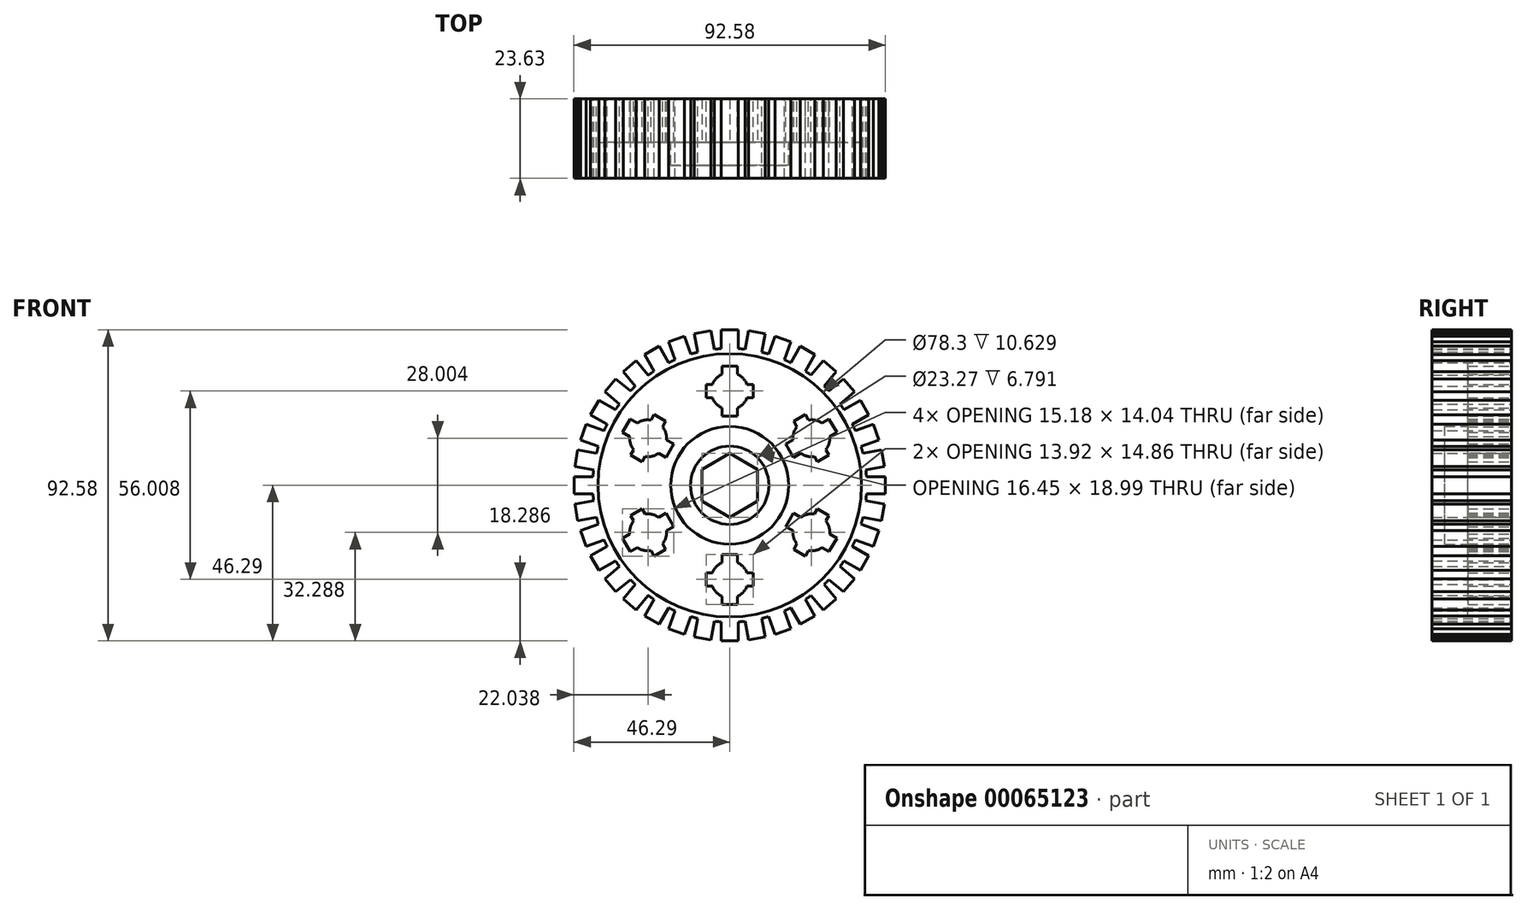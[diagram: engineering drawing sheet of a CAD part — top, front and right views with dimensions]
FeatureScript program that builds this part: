
annotation { "Feature Type Name" : "Feature", "Feature Type Description" : "" }
export const myFeature = defineFeature(function(context is Context, id is Id, definition is map)
    precondition{}
    {
        {
            var Q0;
            Q0=qCreatedBy(makeId("Front.planeOp"),FACE);
            var sketch = newSketch(context, id + "F0", { "sketchPlane" : qUnion([Q0])});
            skCircle(sketch, "E0", {"center": v(0, 0) * mm, "radius": 40.7 * mm});
            skLineSegment(sketch, "E1", {"start": v(-2.5, 40.63) * mm, "end": v(-2.5, 46.29) * mm});
            skLineSegment(sketch, "E2", {"start": v(-2.5, 46.29) * mm, "end": v(0, 46.29) * mm});
            skLineSegment(sketch, "E3", {"start": v(0, 46.29) * mm, "end": v(0, 40.7) * mm});
            skLineSegment(sketch, "E4", {"start": v(0, 40.7) * mm, "end": v(-2.5, 40.63) * mm});
            skLineSegment(sketch, "E5.MirrorCS", {"start": v(2.5, 40.63) * mm, "end": v(2.5, 46.29) * mm});
            skLineSegment(sketch, "E6.MirrorCS", {"start": v(2.5, 46.29) * mm, "end": v(0, 46.29) * mm});
            skLineSegment(sketch, "E7.MirrorCS", {"start": v(0, 40.7) * mm, "end": v(2.5, 40.63) * mm});
            skLineSegment(sketch, "E8.1.0", {"start": v(-4.58, 40.45) * mm, "end": v(-5.57, 46.02) * mm});
            skLineSegment(sketch, "E8.1.1", {"start": v(-10.5, 45.15) * mm, "end": v(-8.04, 45.58) * mm});
            skLineSegment(sketch, "E8.1.2", {"start": v(-8.04, 45.58) * mm, "end": v(-7.07, 40.09) * mm});
            skLineSegment(sketch, "E8.1.3", {"start": v(-5.57, 46.02) * mm, "end": v(-8.04, 45.58) * mm});
            skLineSegment(sketch, "E8.1.4", {"start": v(-9.53, 39.57) * mm, "end": v(-10.5, 45.15) * mm});
            skLineSegment(sketch, "E8.2.0", {"start": v(-11.54, 39.03) * mm, "end": v(-13.47, 44.35) * mm});
            skLineSegment(sketch, "E8.2.1", {"start": v(-18.19, 42.64) * mm, "end": v(-15.83, 43.5) * mm});
            skLineSegment(sketch, "E8.2.2", {"start": v(-15.83, 43.5) * mm, "end": v(-13.92, 38.25) * mm});
            skLineSegment(sketch, "E8.2.3", {"start": v(-13.47, 44.35) * mm, "end": v(-15.83, 43.5) * mm});
            skLineSegment(sketch, "E8.2.4", {"start": v(-16.25, 37.32) * mm, "end": v(-18.19, 42.64) * mm});
            skLineSegment(sketch, "E8.3.0", {"start": v(-18.14, 36.44) * mm, "end": v(-20.97, 41.34) * mm});
            skLineSegment(sketch, "E8.3.1", {"start": v(-25.32, 38.83) * mm, "end": v(-23.14, 40.08) * mm});
            skLineSegment(sketch, "E8.3.2", {"start": v(-23.14, 40.08) * mm, "end": v(-20.35, 35.25) * mm});
            skLineSegment(sketch, "E8.3.3", {"start": v(-20.97, 41.34) * mm, "end": v(-23.14, 40.08) * mm});
            skLineSegment(sketch, "E8.3.4", {"start": v(-22.49, 33.93) * mm, "end": v(-25.32, 38.83) * mm});
            skLineSegment(sketch, "E9.1.4.0", {"start": v(-24.2, 32.73) * mm, "end": v(-27.83, 37.07) * mm});
            skLineSegment(sketch, "E9.3.4.0", {"start": v(-31.67, 33.84) * mm, "end": v(-29.75, 35.46) * mm});
            skLineSegment(sketch, "E9.6.4.0", {"start": v(-29.75, 35.46) * mm, "end": v(-26.16, 31.18) * mm});
            skLineSegment(sketch, "E9.9.4.0", {"start": v(-27.83, 37.07) * mm, "end": v(-29.75, 35.46) * mm});
            skLineSegment(sketch, "E9.12.4.0", {"start": v(-28.04, 29.5) * mm, "end": v(-31.67, 33.84) * mm});
            skLineSegment(sketch, "E9.1.5.0", {"start": v(-29.5, 28.04) * mm, "end": v(-33.84, 31.67) * mm});
            skLineSegment(sketch, "E9.3.5.0", {"start": v(-37.07, 27.83) * mm, "end": v(-35.46, 29.75) * mm});
            skLineSegment(sketch, "E9.6.5.0", {"start": v(-35.46, 29.75) * mm, "end": v(-31.18, 26.16) * mm});
            skLineSegment(sketch, "E9.9.5.0", {"start": v(-33.84, 31.67) * mm, "end": v(-35.46, 29.75) * mm});
            skLineSegment(sketch, "E9.12.5.0", {"start": v(-32.73, 24.2) * mm, "end": v(-37.07, 27.83) * mm});
            skLineSegment(sketch, "E9.1.6.0", {"start": v(-33.93, 22.49) * mm, "end": v(-38.83, 25.32) * mm});
            skLineSegment(sketch, "E9.3.6.0", {"start": v(-41.34, 20.97) * mm, "end": v(-40.08, 23.14) * mm});
            skLineSegment(sketch, "E9.6.6.0", {"start": v(-40.08, 23.14) * mm, "end": v(-35.25, 20.35) * mm});
            skLineSegment(sketch, "E9.9.6.0", {"start": v(-38.83, 25.32) * mm, "end": v(-40.08, 23.14) * mm});
            skLineSegment(sketch, "E9.12.6.0", {"start": v(-36.44, 18.14) * mm, "end": v(-41.34, 20.97) * mm});
            skLineSegment(sketch, "E9.1.7.0", {"start": v(-37.32, 16.25) * mm, "end": v(-42.64, 18.19) * mm});
            skLineSegment(sketch, "E9.3.7.0", {"start": v(-44.35, 13.47) * mm, "end": v(-43.5, 15.83) * mm});
            skLineSegment(sketch, "E9.6.7.0", {"start": v(-43.5, 15.83) * mm, "end": v(-38.25, 13.92) * mm});
            skLineSegment(sketch, "E9.9.7.0", {"start": v(-42.64, 18.19) * mm, "end": v(-43.5, 15.83) * mm});
            skLineSegment(sketch, "E9.12.7.0", {"start": v(-39.03, 11.54) * mm, "end": v(-44.35, 13.47) * mm});
            skLineSegment(sketch, "E9.1.8.0", {"start": v(-39.57, 9.53) * mm, "end": v(-45.15, 10.5) * mm});
            skLineSegment(sketch, "E9.3.8.0", {"start": v(-46.02, 5.57) * mm, "end": v(-45.58, 8.04) * mm});
            skLineSegment(sketch, "E9.6.8.0", {"start": v(-45.58, 8.04) * mm, "end": v(-40.09, 7.07) * mm});
            skLineSegment(sketch, "E9.9.8.0", {"start": v(-45.15, 10.5) * mm, "end": v(-45.58, 8.04) * mm});
            skLineSegment(sketch, "E9.12.8.0", {"start": v(-40.45, 4.58) * mm, "end": v(-46.02, 5.57) * mm});
            skLineSegment(sketch, "E9.1.9.0", {"start": v(-40.63, 2.5) * mm, "end": v(-46.29, 2.5) * mm});
            skLineSegment(sketch, "E9.3.9.0", {"start": v(-46.29, -2.5) * mm, "end": v(-46.29, 0) * mm});
            skLineSegment(sketch, "E9.6.9.0", {"start": v(-46.29, 0) * mm, "end": v(-40.7, 0) * mm});
            skLineSegment(sketch, "E9.9.9.0", {"start": v(-46.29, 2.5) * mm, "end": v(-46.29, 0) * mm});
            skLineSegment(sketch, "E9.12.9.0", {"start": v(-40.63, -2.5) * mm, "end": v(-46.29, -2.5) * mm});
            skLineSegment(sketch, "E9.1.10.0", {"start": v(-40.45, -4.58) * mm, "end": v(-46.02, -5.57) * mm});
            skLineSegment(sketch, "E9.3.10.0", {"start": v(-45.15, -10.5) * mm, "end": v(-45.58, -8.04) * mm});
            skLineSegment(sketch, "E9.6.10.0", {"start": v(-45.58, -8.04) * mm, "end": v(-40.09, -7.07) * mm});
            skLineSegment(sketch, "E9.9.10.0", {"start": v(-46.02, -5.57) * mm, "end": v(-45.58, -8.04) * mm});
            skLineSegment(sketch, "E9.12.10.0", {"start": v(-39.57, -9.53) * mm, "end": v(-45.15, -10.5) * mm});
            skLineSegment(sketch, "E9.1.11.0", {"start": v(-39.03, -11.54) * mm, "end": v(-44.35, -13.47) * mm});
            skLineSegment(sketch, "E9.3.11.0", {"start": v(-42.64, -18.19) * mm, "end": v(-43.5, -15.83) * mm});
            skLineSegment(sketch, "E9.6.11.0", {"start": v(-43.5, -15.83) * mm, "end": v(-38.25, -13.92) * mm});
            skLineSegment(sketch, "E9.9.11.0", {"start": v(-44.35, -13.47) * mm, "end": v(-43.5, -15.83) * mm});
            skLineSegment(sketch, "E9.12.11.0", {"start": v(-37.32, -16.25) * mm, "end": v(-42.64, -18.19) * mm});
            skLineSegment(sketch, "E10.1.12.0", {"start": v(-36.44, -18.14) * mm, "end": v(-41.34, -20.97) * mm});
            skLineSegment(sketch, "E10.3.12.0", {"start": v(-38.83, -25.32) * mm, "end": v(-40.08, -23.14) * mm});
            skLineSegment(sketch, "E10.6.12.0", {"start": v(-40.08, -23.14) * mm, "end": v(-35.25, -20.35) * mm});
            skLineSegment(sketch, "E10.9.12.0", {"start": v(-41.34, -20.97) * mm, "end": v(-40.08, -23.14) * mm});
            skLineSegment(sketch, "E10.12.12.0", {"start": v(-33.93, -22.49) * mm, "end": v(-38.83, -25.32) * mm});
            skLineSegment(sketch, "E10.1.13.0", {"start": v(-32.73, -24.2) * mm, "end": v(-37.07, -27.83) * mm});
            skLineSegment(sketch, "E10.3.13.0", {"start": v(-33.84, -31.67) * mm, "end": v(-35.46, -29.75) * mm});
            skLineSegment(sketch, "E10.6.13.0", {"start": v(-35.46, -29.75) * mm, "end": v(-31.18, -26.16) * mm});
            skLineSegment(sketch, "E10.9.13.0", {"start": v(-37.07, -27.83) * mm, "end": v(-35.46, -29.75) * mm});
            skLineSegment(sketch, "E10.12.13.0", {"start": v(-29.5, -28.04) * mm, "end": v(-33.84, -31.67) * mm});
            skLineSegment(sketch, "E10.1.14.0", {"start": v(-28.04, -29.5) * mm, "end": v(-31.67, -33.84) * mm});
            skLineSegment(sketch, "E10.3.14.0", {"start": v(-27.83, -37.07) * mm, "end": v(-29.75, -35.46) * mm});
            skLineSegment(sketch, "E10.6.14.0", {"start": v(-29.75, -35.46) * mm, "end": v(-26.16, -31.18) * mm});
            skLineSegment(sketch, "E10.9.14.0", {"start": v(-31.67, -33.84) * mm, "end": v(-29.75, -35.46) * mm});
            skLineSegment(sketch, "E10.12.14.0", {"start": v(-24.2, -32.73) * mm, "end": v(-27.83, -37.07) * mm});
            skLineSegment(sketch, "E10.1.15.0", {"start": v(-22.49, -33.93) * mm, "end": v(-25.32, -38.83) * mm});
            skLineSegment(sketch, "E10.3.15.0", {"start": v(-20.97, -41.34) * mm, "end": v(-23.14, -40.08) * mm});
            skLineSegment(sketch, "E10.6.15.0", {"start": v(-23.14, -40.08) * mm, "end": v(-20.35, -35.25) * mm});
            skLineSegment(sketch, "E10.9.15.0", {"start": v(-25.32, -38.83) * mm, "end": v(-23.14, -40.08) * mm});
            skLineSegment(sketch, "E10.12.15.0", {"start": v(-18.14, -36.44) * mm, "end": v(-20.97, -41.34) * mm});
            skLineSegment(sketch, "E10.1.16.0", {"start": v(-16.25, -37.32) * mm, "end": v(-18.19, -42.64) * mm});
            skLineSegment(sketch, "E10.3.16.0", {"start": v(-13.47, -44.35) * mm, "end": v(-15.83, -43.5) * mm});
            skLineSegment(sketch, "E10.6.16.0", {"start": v(-15.83, -43.5) * mm, "end": v(-13.92, -38.25) * mm});
            skLineSegment(sketch, "E10.9.16.0", {"start": v(-18.19, -42.64) * mm, "end": v(-15.83, -43.5) * mm});
            skLineSegment(sketch, "E10.12.16.0", {"start": v(-11.54, -39.03) * mm, "end": v(-13.47, -44.35) * mm});
            skLineSegment(sketch, "E10.1.17.0", {"start": v(-9.53, -39.57) * mm, "end": v(-10.5, -45.15) * mm});
            skLineSegment(sketch, "E10.3.17.0", {"start": v(-5.57, -46.02) * mm, "end": v(-8.04, -45.58) * mm});
            skLineSegment(sketch, "E10.6.17.0", {"start": v(-8.04, -45.58) * mm, "end": v(-7.07, -40.09) * mm});
            skLineSegment(sketch, "E10.9.17.0", {"start": v(-10.5, -45.15) * mm, "end": v(-8.04, -45.58) * mm});
            skLineSegment(sketch, "E10.12.17.0", {"start": v(-4.58, -40.45) * mm, "end": v(-5.57, -46.02) * mm});
            skLineSegment(sketch, "E10.1.18.0", {"start": v(-2.5, -40.63) * mm, "end": v(-2.5, -46.29) * mm});
            skLineSegment(sketch, "E10.3.18.0", {"start": v(2.5, -46.29) * mm, "end": v(0, -46.29) * mm});
            skLineSegment(sketch, "E10.6.18.0", {"start": v(0, -46.29) * mm, "end": v(0, -40.7) * mm});
            skLineSegment(sketch, "E10.9.18.0", {"start": v(-2.5, -46.29) * mm, "end": v(0, -46.29) * mm});
            skLineSegment(sketch, "E10.12.18.0", {"start": v(2.5, -40.63) * mm, "end": v(2.5, -46.29) * mm});
            skLineSegment(sketch, "E10.1.19.0", {"start": v(4.58, -40.45) * mm, "end": v(5.57, -46.02) * mm});
            skLineSegment(sketch, "E10.3.19.0", {"start": v(10.5, -45.15) * mm, "end": v(8.04, -45.58) * mm});
            skLineSegment(sketch, "E10.6.19.0", {"start": v(8.04, -45.58) * mm, "end": v(7.07, -40.09) * mm});
            skLineSegment(sketch, "E10.9.19.0", {"start": v(5.57, -46.02) * mm, "end": v(8.04, -45.58) * mm});
            skLineSegment(sketch, "E10.12.19.0", {"start": v(9.53, -39.57) * mm, "end": v(10.5, -45.15) * mm});
            skLineSegment(sketch, "E10.1.20.0", {"start": v(11.54, -39.03) * mm, "end": v(13.47, -44.35) * mm});
            skLineSegment(sketch, "E10.3.20.0", {"start": v(18.19, -42.64) * mm, "end": v(15.83, -43.5) * mm});
            skLineSegment(sketch, "E10.6.20.0", {"start": v(15.83, -43.5) * mm, "end": v(13.92, -38.25) * mm});
            skLineSegment(sketch, "E10.9.20.0", {"start": v(13.47, -44.35) * mm, "end": v(15.83, -43.5) * mm});
            skLineSegment(sketch, "E10.12.20.0", {"start": v(16.25, -37.32) * mm, "end": v(18.19, -42.64) * mm});
            skLineSegment(sketch, "E10.1.21.0", {"start": v(18.14, -36.44) * mm, "end": v(20.97, -41.34) * mm});
            skLineSegment(sketch, "E10.3.21.0", {"start": v(25.32, -38.83) * mm, "end": v(23.14, -40.08) * mm});
            skLineSegment(sketch, "E10.6.21.0", {"start": v(23.14, -40.08) * mm, "end": v(20.35, -35.25) * mm});
            skLineSegment(sketch, "E10.9.21.0", {"start": v(20.97, -41.34) * mm, "end": v(23.14, -40.08) * mm});
            skLineSegment(sketch, "E10.12.21.0", {"start": v(22.49, -33.93) * mm, "end": v(25.32, -38.83) * mm});
            skLineSegment(sketch, "E10.1.22.0", {"start": v(24.2, -32.73) * mm, "end": v(27.83, -37.07) * mm});
            skLineSegment(sketch, "E10.3.22.0", {"start": v(31.67, -33.84) * mm, "end": v(29.75, -35.46) * mm});
            skLineSegment(sketch, "E10.6.22.0", {"start": v(29.75, -35.46) * mm, "end": v(26.16, -31.18) * mm});
            skLineSegment(sketch, "E10.9.22.0", {"start": v(27.83, -37.07) * mm, "end": v(29.75, -35.46) * mm});
            skLineSegment(sketch, "E10.12.22.0", {"start": v(28.04, -29.5) * mm, "end": v(31.67, -33.84) * mm});
            skLineSegment(sketch, "E10.1.23.0", {"start": v(29.5, -28.04) * mm, "end": v(33.84, -31.67) * mm});
            skLineSegment(sketch, "E10.3.23.0", {"start": v(37.07, -27.83) * mm, "end": v(35.46, -29.75) * mm});
            skLineSegment(sketch, "E10.6.23.0", {"start": v(35.46, -29.75) * mm, "end": v(31.18, -26.16) * mm});
            skLineSegment(sketch, "E10.9.23.0", {"start": v(33.84, -31.67) * mm, "end": v(35.46, -29.75) * mm});
            skLineSegment(sketch, "E10.12.23.0", {"start": v(32.73, -24.2) * mm, "end": v(37.07, -27.83) * mm});
            skLineSegment(sketch, "E11.1.24.0", {"start": v(33.93, -22.49) * mm, "end": v(38.83, -25.32) * mm});
            skLineSegment(sketch, "E11.3.24.0", {"start": v(41.34, -20.97) * mm, "end": v(40.08, -23.14) * mm});
            skLineSegment(sketch, "E11.6.24.0", {"start": v(40.08, -23.14) * mm, "end": v(35.25, -20.35) * mm});
            skLineSegment(sketch, "E11.9.24.0", {"start": v(38.83, -25.32) * mm, "end": v(40.08, -23.14) * mm});
            skLineSegment(sketch, "E11.12.24.0", {"start": v(36.44, -18.14) * mm, "end": v(41.34, -20.97) * mm});
            skLineSegment(sketch, "E11.1.25.0", {"start": v(37.32, -16.25) * mm, "end": v(42.64, -18.19) * mm});
            skLineSegment(sketch, "E11.3.25.0", {"start": v(44.35, -13.47) * mm, "end": v(43.5, -15.83) * mm});
            skLineSegment(sketch, "E11.6.25.0", {"start": v(43.5, -15.83) * mm, "end": v(38.25, -13.92) * mm});
            skLineSegment(sketch, "E11.9.25.0", {"start": v(42.64, -18.19) * mm, "end": v(43.5, -15.83) * mm});
            skLineSegment(sketch, "E11.12.25.0", {"start": v(39.03, -11.54) * mm, "end": v(44.35, -13.47) * mm});
            skLineSegment(sketch, "E11.1.26.0", {"start": v(39.57, -9.53) * mm, "end": v(45.15, -10.5) * mm});
            skLineSegment(sketch, "E11.3.26.0", {"start": v(46.02, -5.57) * mm, "end": v(45.58, -8.04) * mm});
            skLineSegment(sketch, "E11.6.26.0", {"start": v(45.58, -8.04) * mm, "end": v(40.09, -7.07) * mm});
            skLineSegment(sketch, "E11.9.26.0", {"start": v(45.15, -10.5) * mm, "end": v(45.58, -8.04) * mm});
            skLineSegment(sketch, "E11.12.26.0", {"start": v(40.45, -4.58) * mm, "end": v(46.02, -5.57) * mm});
            skLineSegment(sketch, "E11.1.27.0", {"start": v(40.63, -2.5) * mm, "end": v(46.29, -2.5) * mm});
            skLineSegment(sketch, "E11.3.27.0", {"start": v(46.29, 2.5) * mm, "end": v(46.29, 0) * mm});
            skLineSegment(sketch, "E11.6.27.0", {"start": v(46.29, 0) * mm, "end": v(40.7, 0) * mm});
            skLineSegment(sketch, "E11.9.27.0", {"start": v(46.29, -2.5) * mm, "end": v(46.29, 0) * mm});
            skLineSegment(sketch, "E11.12.27.0", {"start": v(40.63, 2.5) * mm, "end": v(46.29, 2.5) * mm});
            skLineSegment(sketch, "E11.1.28.0", {"start": v(40.45, 4.58) * mm, "end": v(46.02, 5.57) * mm});
            skLineSegment(sketch, "E11.3.28.0", {"start": v(45.15, 10.5) * mm, "end": v(45.58, 8.04) * mm});
            skLineSegment(sketch, "E11.6.28.0", {"start": v(45.58, 8.04) * mm, "end": v(40.09, 7.07) * mm});
            skLineSegment(sketch, "E11.9.28.0", {"start": v(46.02, 5.57) * mm, "end": v(45.58, 8.04) * mm});
            skLineSegment(sketch, "E11.12.28.0", {"start": v(39.57, 9.53) * mm, "end": v(45.15, 10.5) * mm});
            skLineSegment(sketch, "E11.1.29.0", {"start": v(39.03, 11.54) * mm, "end": v(44.35, 13.47) * mm});
            skLineSegment(sketch, "E11.3.29.0", {"start": v(42.64, 18.19) * mm, "end": v(43.5, 15.83) * mm});
            skLineSegment(sketch, "E11.6.29.0", {"start": v(43.5, 15.83) * mm, "end": v(38.25, 13.92) * mm});
            skLineSegment(sketch, "E11.9.29.0", {"start": v(44.35, 13.47) * mm, "end": v(43.5, 15.83) * mm});
            skLineSegment(sketch, "E11.12.29.0", {"start": v(37.32, 16.25) * mm, "end": v(42.64, 18.19) * mm});
            skLineSegment(sketch, "E11.1.30.0", {"start": v(36.44, 18.14) * mm, "end": v(41.34, 20.97) * mm});
            skLineSegment(sketch, "E11.3.30.0", {"start": v(38.83, 25.32) * mm, "end": v(40.08, 23.14) * mm});
            skLineSegment(sketch, "E11.6.30.0", {"start": v(40.08, 23.14) * mm, "end": v(35.25, 20.35) * mm});
            skLineSegment(sketch, "E11.9.30.0", {"start": v(41.34, 20.97) * mm, "end": v(40.08, 23.14) * mm});
            skLineSegment(sketch, "E11.12.30.0", {"start": v(33.93, 22.49) * mm, "end": v(38.83, 25.32) * mm});
            skLineSegment(sketch, "E11.1.31.0", {"start": v(32.73, 24.2) * mm, "end": v(37.07, 27.83) * mm});
            skLineSegment(sketch, "E11.3.31.0", {"start": v(33.84, 31.67) * mm, "end": v(35.46, 29.75) * mm});
            skLineSegment(sketch, "E11.6.31.0", {"start": v(35.46, 29.75) * mm, "end": v(31.18, 26.16) * mm});
            skLineSegment(sketch, "E11.9.31.0", {"start": v(37.07, 27.83) * mm, "end": v(35.46, 29.75) * mm});
            skLineSegment(sketch, "E11.12.31.0", {"start": v(29.5, 28.04) * mm, "end": v(33.84, 31.67) * mm});
            skLineSegment(sketch, "E11.1.32.0", {"start": v(28.04, 29.5) * mm, "end": v(31.67, 33.84) * mm});
            skLineSegment(sketch, "E11.3.32.0", {"start": v(27.83, 37.07) * mm, "end": v(29.75, 35.46) * mm});
            skLineSegment(sketch, "E11.6.32.0", {"start": v(29.75, 35.46) * mm, "end": v(26.16, 31.18) * mm});
            skLineSegment(sketch, "E11.9.32.0", {"start": v(31.67, 33.84) * mm, "end": v(29.75, 35.46) * mm});
            skLineSegment(sketch, "E11.12.32.0", {"start": v(24.2, 32.73) * mm, "end": v(27.83, 37.07) * mm});
            skLineSegment(sketch, "E11.1.33.0", {"start": v(22.49, 33.93) * mm, "end": v(25.32, 38.83) * mm});
            skLineSegment(sketch, "E11.3.33.0", {"start": v(20.97, 41.34) * mm, "end": v(23.14, 40.08) * mm});
            skLineSegment(sketch, "E11.6.33.0", {"start": v(23.14, 40.08) * mm, "end": v(20.35, 35.25) * mm});
            skLineSegment(sketch, "E11.9.33.0", {"start": v(25.32, 38.83) * mm, "end": v(23.14, 40.08) * mm});
            skLineSegment(sketch, "E11.12.33.0", {"start": v(18.14, 36.44) * mm, "end": v(20.97, 41.34) * mm});
            skLineSegment(sketch, "E11.1.34.0", {"start": v(16.25, 37.32) * mm, "end": v(18.19, 42.64) * mm});
            skLineSegment(sketch, "E11.3.34.0", {"start": v(13.47, 44.35) * mm, "end": v(15.83, 43.5) * mm});
            skLineSegment(sketch, "E11.6.34.0", {"start": v(15.83, 43.5) * mm, "end": v(13.92, 38.25) * mm});
            skLineSegment(sketch, "E11.9.34.0", {"start": v(18.19, 42.64) * mm, "end": v(15.83, 43.5) * mm});
            skLineSegment(sketch, "E11.12.34.0", {"start": v(11.54, 39.03) * mm, "end": v(13.47, 44.35) * mm});
            skLineSegment(sketch, "E11.1.35.0", {"start": v(9.53, 39.57) * mm, "end": v(10.5, 45.15) * mm});
            skLineSegment(sketch, "E11.3.35.0", {"start": v(5.57, 46.02) * mm, "end": v(8.04, 45.58) * mm});
            skLineSegment(sketch, "E11.6.35.0", {"start": v(8.04, 45.58) * mm, "end": v(7.07, 40.09) * mm});
            skLineSegment(sketch, "E11.9.35.0", {"start": v(10.5, 45.15) * mm, "end": v(8.04, 45.58) * mm});
            skLineSegment(sketch, "E11.12.35.0", {"start": v(4.58, 40.45) * mm, "end": v(5.57, 46.02) * mm});
            skArc(sketch, "E12", {"start": v(-2.31, 32.99) * mm, "mid": v(-4, 31.76) * mm, "end": v(-5.12, 30) * mm});
            skLineSegment(sketch, "E13.rect.bottom", {"start": v(6.96, 26.02) * mm, "end": v(5.12, 26.02) * mm});
            skLineSegment(sketch, "E13.rect.top", {"start": v(6.96, 30) * mm, "end": v(5.12, 30) * mm});
            skLineSegment(sketch, "E13.rect.left", {"start": v(6.96, 26.02) * mm, "end": v(6.96, 30) * mm});
            skLineSegment(sketch, "E13.rect.right", {"start": v(-6.96, 26.02) * mm, "end": v(-6.96, 30) * mm});
            skLineSegment(sketch, "E14.rect.bottom", {"start": v(2.31, 35.43) * mm, "end": v(-2.31, 35.43) * mm});
            skLineSegment(sketch, "E14.rect.top", {"start": v(2.31, 20.57) * mm, "end": v(-2.31, 20.57) * mm});
            skLineSegment(sketch, "E14.rect.right", {"start": v(-2.31, 35.43) * mm, "end": v(-2.31, 32.99) * mm});
            skLineSegment(sketch, "E15.trimOffspring", {"start": v(-5.12, 30) * mm, "end": v(-6.96, 30) * mm});
            skLineSegment(sketch, "E16.trimOffspring", {"start": v(-2.31, 23.02) * mm, "end": v(-2.31, 20.57) * mm});
            skArc(sketch, "E17.trimOffspring", {"start": v(-5.12, 26.02) * mm, "mid": v(-4, 24.25) * mm, "end": v(-2.31, 23.02) * mm});
            skLineSegment(sketch, "E18.trimOffspring", {"start": v(2.31, 23.02) * mm, "end": v(2.31, 20.57) * mm});
            skArc(sketch, "E19.trimOffspring", {"start": v(5.12, 30) * mm, "mid": v(4, 31.76) * mm, "end": v(2.31, 32.99) * mm});
            skLineSegment(sketch, "E20.trimOffspring", {"start": v(-5.12, 26.02) * mm, "end": v(-6.96, 26.02) * mm});
            skArc(sketch, "E21.trimOffspring", {"start": v(2.31, 23.02) * mm, "mid": v(4, 24.25) * mm, "end": v(5.12, 26.02) * mm});
            skLineSegment(sketch, "E22", {"start": v(2.31, 32.99) * mm, "end": v(2.31, 35.43) * mm});
            skLineSegment(sketch, "E23.1.0", {"start": v(-26.01, 6.98) * mm, "end": v(-29.45, 8.97) * mm});
            skLineSegment(sketch, "E23.1.1", {"start": v(-16.66, 12.3) * mm, "end": v(-18.97, 8.28) * mm});
            skLineSegment(sketch, "E23.1.2", {"start": v(-29.53, 19.72) * mm, "end": v(-31.84, 15.71) * mm});
            skLineSegment(sketch, "E23.1.3", {"start": v(-19.05, 19.04) * mm, "end": v(-22.5, 21.02) * mm});
            skArc(sketch, "E23.1.4", {"start": v(-29.72, 14.49) * mm, "mid": v(-29.5, 12.4) * mm, "end": v(-28.53, 10.56) * mm});
            skArc(sketch, "E23.1.5", {"start": v(-18.78, 13.51) * mm, "mid": v(-19, 15.6) * mm, "end": v(-19.97, 17.44) * mm});
            skPoint(sketch, "E23.1.6", {"position": v(-24.25, 14) * mm});
            skArc(sketch, "E23.1.7", {"start": v(-25.1, 8.57) * mm, "mid": v(-23, 8.65) * mm, "end": v(-21.1, 9.5) * mm});
            skArc(sketch, "E23.1.8", {"start": v(-23.41, 19.43) * mm, "mid": v(-25.5, 19.35) * mm, "end": v(-27.41, 18.5) * mm});
            skPoint(sketch, "E23.1.9", {"position": v(-24.25, 14) * mm});
            skLineSegment(sketch, "E23.1.10", {"start": v(-22.5, 21.02) * mm, "end": v(-23.41, 19.43) * mm});
            skLineSegment(sketch, "E23.1.11", {"start": v(-18.78, 13.51) * mm, "end": v(-16.66, 12.3) * mm});
            skLineSegment(sketch, "E23.1.12", {"start": v(-19.05, 19.04) * mm, "end": v(-19.97, 17.44) * mm});
            skLineSegment(sketch, "E23.1.13", {"start": v(-27.41, 18.5) * mm, "end": v(-29.53, 19.72) * mm});
            skLineSegment(sketch, "E23.1.14", {"start": v(-25.1, 8.57) * mm, "end": v(-26.01, 6.98) * mm});
            skLineSegment(sketch, "E23.1.15", {"start": v(-31.84, 15.71) * mm, "end": v(-29.72, 14.49) * mm});
            skLineSegment(sketch, "E23.1.16", {"start": v(-28.53, 10.56) * mm, "end": v(-29.45, 8.97) * mm});
            skLineSegment(sketch, "E23.1.17", {"start": v(-21.1, 9.5) * mm, "end": v(-18.97, 8.28) * mm});
            skLineSegment(sketch, "E23.2.0", {"start": v(-19.05, -19.04) * mm, "end": v(-22.5, -21.02) * mm});
            skLineSegment(sketch, "E23.2.1", {"start": v(-18.97, -8.28) * mm, "end": v(-16.66, -12.3) * mm});
            skLineSegment(sketch, "E23.2.2", {"start": v(-31.84, -15.71) * mm, "end": v(-29.53, -19.72) * mm});
            skLineSegment(sketch, "E23.2.3", {"start": v(-26.01, -6.98) * mm, "end": v(-29.45, -8.97) * mm});
            skArc(sketch, "E23.2.4", {"start": v(-27.41, -18.5) * mm, "mid": v(-25.5, -19.35) * mm, "end": v(-23.41, -19.43) * mm});
            skArc(sketch, "E23.2.5", {"start": v(-21.1, -9.5) * mm, "mid": v(-23, -8.65) * mm, "end": v(-25.1, -8.57) * mm});
            skPoint(sketch, "E23.2.6", {"position": v(-24.25, -14) * mm});
            skArc(sketch, "E23.2.7", {"start": v(-19.97, -17.44) * mm, "mid": v(-19, -15.6) * mm, "end": v(-18.78, -13.51) * mm});
            skArc(sketch, "E23.2.8", {"start": v(-28.53, -10.56) * mm, "mid": v(-29.5, -12.4) * mm, "end": v(-29.72, -14.49) * mm});
            skPoint(sketch, "E23.2.9", {"position": v(-24.25, -14) * mm});
            skLineSegment(sketch, "E23.2.10", {"start": v(-29.45, -8.97) * mm, "end": v(-28.53, -10.56) * mm});
            skLineSegment(sketch, "E23.2.11", {"start": v(-21.1, -9.5) * mm, "end": v(-18.97, -8.28) * mm});
            skLineSegment(sketch, "E23.2.12", {"start": v(-26.01, -6.98) * mm, "end": v(-25.1, -8.57) * mm});
            skLineSegment(sketch, "E23.2.13", {"start": v(-29.72, -14.49) * mm, "end": v(-31.84, -15.71) * mm});
            skLineSegment(sketch, "E23.2.14", {"start": v(-19.97, -17.44) * mm, "end": v(-19.05, -19.04) * mm});
            skLineSegment(sketch, "E23.2.15", {"start": v(-29.53, -19.72) * mm, "end": v(-27.41, -18.5) * mm});
            skLineSegment(sketch, "E23.2.16", {"start": v(-23.41, -19.43) * mm, "end": v(-22.5, -21.02) * mm});
            skLineSegment(sketch, "E23.2.17", {"start": v(-18.78, -13.51) * mm, "end": v(-16.66, -12.3) * mm});
            skLineSegment(sketch, "E23.3.0", {"start": v(6.96, -26.02) * mm, "end": v(6.96, -30) * mm});
            skLineSegment(sketch, "E23.3.1", {"start": v(-2.31, -20.57) * mm, "end": v(2.31, -20.57) * mm});
            skLineSegment(sketch, "E23.3.2", {"start": v(-2.31, -35.43) * mm, "end": v(2.31, -35.43) * mm});
            skLineSegment(sketch, "E23.3.3", {"start": v(-6.96, -26.02) * mm, "end": v(-6.96, -30) * mm});
            skArc(sketch, "E23.3.4", {"start": v(2.31, -32.99) * mm, "mid": v(4, -31.76) * mm, "end": v(5.12, -30) * mm});
            skArc(sketch, "E23.3.5", {"start": v(-2.31, -23.02) * mm, "mid": v(-4, -24.25) * mm, "end": v(-5.12, -26.02) * mm});
            skPoint(sketch, "E23.3.6", {"position": v(0, -28) * mm});
            skArc(sketch, "E23.3.7", {"start": v(5.12, -26.02) * mm, "mid": v(4, -24.25) * mm, "end": v(2.31, -23.02) * mm});
            skArc(sketch, "E23.3.8", {"start": v(-5.12, -30) * mm, "mid": v(-4, -31.76) * mm, "end": v(-2.31, -32.99) * mm});
            skPoint(sketch, "E23.3.9", {"position": v(0, -28) * mm});
            skLineSegment(sketch, "E23.3.10", {"start": v(-6.96, -30) * mm, "end": v(-5.12, -30) * mm});
            skLineSegment(sketch, "E23.3.11", {"start": v(-2.31, -23.02) * mm, "end": v(-2.31, -20.57) * mm});
            skLineSegment(sketch, "E23.3.12", {"start": v(-6.96, -26.02) * mm, "end": v(-5.12, -26.02) * mm});
            skLineSegment(sketch, "E23.3.13", {"start": v(-2.31, -32.99) * mm, "end": v(-2.31, -35.43) * mm});
            skLineSegment(sketch, "E23.3.14", {"start": v(5.12, -26.02) * mm, "end": v(6.96, -26.02) * mm});
            skLineSegment(sketch, "E23.3.15", {"start": v(2.31, -35.43) * mm, "end": v(2.31, -32.99) * mm});
            skLineSegment(sketch, "E23.3.16", {"start": v(5.12, -30) * mm, "end": v(6.96, -30) * mm});
            skLineSegment(sketch, "E23.3.17", {"start": v(2.31, -23.02) * mm, "end": v(2.31, -20.57) * mm});
            skLineSegment(sketch, "E23.4.0", {"start": v(26.01, -6.98) * mm, "end": v(29.45, -8.97) * mm});
            skLineSegment(sketch, "E23.4.1", {"start": v(16.66, -12.3) * mm, "end": v(18.97, -8.28) * mm});
            skLineSegment(sketch, "E23.4.2", {"start": v(29.53, -19.72) * mm, "end": v(31.84, -15.71) * mm});
            skLineSegment(sketch, "E23.4.3", {"start": v(19.05, -19.04) * mm, "end": v(22.5, -21.02) * mm});
            skArc(sketch, "E23.4.4", {"start": v(29.72, -14.49) * mm, "mid": v(29.5, -12.4) * mm, "end": v(28.53, -10.56) * mm});
            skArc(sketch, "E23.4.5", {"start": v(18.78, -13.51) * mm, "mid": v(19, -15.6) * mm, "end": v(19.97, -17.44) * mm});
            skPoint(sketch, "E23.4.6", {"position": v(24.25, -14) * mm});
            skArc(sketch, "E23.4.7", {"start": v(25.1, -8.57) * mm, "mid": v(23, -8.65) * mm, "end": v(21.1, -9.5) * mm});
            skArc(sketch, "E23.4.8", {"start": v(23.41, -19.43) * mm, "mid": v(25.5, -19.35) * mm, "end": v(27.41, -18.5) * mm});
            skPoint(sketch, "E23.4.9", {"position": v(24.25, -14) * mm});
            skLineSegment(sketch, "E23.4.10", {"start": v(22.5, -21.02) * mm, "end": v(23.41, -19.43) * mm});
            skLineSegment(sketch, "E23.4.11", {"start": v(18.78, -13.51) * mm, "end": v(16.66, -12.3) * mm});
            skLineSegment(sketch, "E23.4.12", {"start": v(19.05, -19.04) * mm, "end": v(19.97, -17.44) * mm});
            skLineSegment(sketch, "E23.4.13", {"start": v(27.41, -18.5) * mm, "end": v(29.53, -19.72) * mm});
            skLineSegment(sketch, "E23.4.14", {"start": v(25.1, -8.57) * mm, "end": v(26.01, -6.98) * mm});
            skLineSegment(sketch, "E23.4.15", {"start": v(31.84, -15.71) * mm, "end": v(29.72, -14.49) * mm});
            skLineSegment(sketch, "E23.4.16", {"start": v(28.53, -10.56) * mm, "end": v(29.45, -8.97) * mm});
            skLineSegment(sketch, "E23.4.17", {"start": v(21.1, -9.5) * mm, "end": v(18.97, -8.28) * mm});
            skLineSegment(sketch, "E23.5.0", {"start": v(19.05, 19.04) * mm, "end": v(22.5, 21.02) * mm});
            skLineSegment(sketch, "E23.5.1", {"start": v(18.97, 8.28) * mm, "end": v(16.66, 12.3) * mm});
            skLineSegment(sketch, "E23.5.2", {"start": v(31.84, 15.71) * mm, "end": v(29.53, 19.72) * mm});
            skLineSegment(sketch, "E23.5.3", {"start": v(26.01, 6.98) * mm, "end": v(29.45, 8.97) * mm});
            skArc(sketch, "E23.5.4", {"start": v(27.41, 18.5) * mm, "mid": v(25.5, 19.35) * mm, "end": v(23.41, 19.43) * mm});
            skArc(sketch, "E23.5.5", {"start": v(21.1, 9.5) * mm, "mid": v(23, 8.65) * mm, "end": v(25.1, 8.57) * mm});
            skPoint(sketch, "E23.5.6", {"position": v(24.25, 14) * mm});
            skArc(sketch, "E23.5.7", {"start": v(19.97, 17.44) * mm, "mid": v(19, 15.6) * mm, "end": v(18.78, 13.51) * mm});
            skArc(sketch, "E23.5.8", {"start": v(28.53, 10.56) * mm, "mid": v(29.5, 12.4) * mm, "end": v(29.72, 14.49) * mm});
            skPoint(sketch, "E23.5.9", {"position": v(24.25, 14) * mm});
            skLineSegment(sketch, "E23.5.10", {"start": v(29.45, 8.97) * mm, "end": v(28.53, 10.56) * mm});
            skLineSegment(sketch, "E23.5.11", {"start": v(21.1, 9.5) * mm, "end": v(18.97, 8.28) * mm});
            skLineSegment(sketch, "E23.5.12", {"start": v(26.01, 6.98) * mm, "end": v(25.1, 8.57) * mm});
            skLineSegment(sketch, "E23.5.13", {"start": v(29.72, 14.49) * mm, "end": v(31.84, 15.71) * mm});
            skLineSegment(sketch, "E23.5.14", {"start": v(19.97, 17.44) * mm, "end": v(19.05, 19.04) * mm});
            skLineSegment(sketch, "E23.5.15", {"start": v(29.53, 19.72) * mm, "end": v(27.41, 18.5) * mm});
            skLineSegment(sketch, "E23.5.16", {"start": v(23.41, 19.43) * mm, "end": v(22.5, 21.02) * mm});
            skLineSegment(sketch, "E23.5.17", {"start": v(18.78, 13.51) * mm, "end": v(16.66, 12.3) * mm});
            skSolve(sketch);
        }
        {
            var Q0;
            {var subQ53=sQuery(id+"F0.wireOp",EDGE,"E4");Q0=makeQuery(id+"F0.imprint","IMPRINT",FACE,{"disambiguationData":[TD([[makeQuery(id+"F0.imprint","IMPRINT",EDGE,{"derivedFrom":subQ53}),1.0]])]});}
            var Q1;
            Q1=makeQuery(id+"F0.imprint","IMPRINT",FACE,{"disambiguationData":[TD([[makeQuery(id+"F0.imprint","IMPRINT",EDGE,{"derivedFrom":sQuery(id+"F0.wireOp",EDGE,"E11.3.27.0")}),-1.0]])]});
            var Q2;
            {var subQ0=sQuery(id+"F0.wireOp",EDGE,"E11.1.28.0");Q2=makeQuery(id+"F0.imprint","IMPRINT",FACE,{"disambiguationData":[TD([[makeQuery(id+"F0.imprint","IMPRINT",EDGE,{"derivedFrom":subQ0}),1.0]])]});}
            var Q3;
            Q3=makeQuery(id+"F0.imprint","IMPRINT",FACE,{"disambiguationData":[TD([[makeQuery(id+"F0.imprint","IMPRINT",EDGE,{"derivedFrom":sQuery(id+"F0.wireOp",EDGE,"E11.3.28.0")}),-1.0]])]});
            var Q4;
            {var subQ0=sQuery(id+"F0.wireOp",EDGE,"E11.1.29.0");Q4=makeQuery(id+"F0.imprint","IMPRINT",FACE,{"disambiguationData":[TD([[makeQuery(id+"F0.imprint","IMPRINT",EDGE,{"derivedFrom":subQ0}),1.0]])]});}
            var Q5;
            Q5=makeQuery(id+"F0.imprint","IMPRINT",FACE,{"disambiguationData":[TD([[makeQuery(id+"F0.imprint","IMPRINT",EDGE,{"derivedFrom":sQuery(id+"F0.wireOp",EDGE,"E11.3.29.0")}),-1.0]])]});
            var Q6;
            {var subQ0=sQuery(id+"F0.wireOp",EDGE,"E11.1.30.0");Q6=makeQuery(id+"F0.imprint","IMPRINT",FACE,{"disambiguationData":[TD([[makeQuery(id+"F0.imprint","IMPRINT",EDGE,{"derivedFrom":subQ0}),1.0]])]});}
            var Q7;
            Q7=makeQuery(id+"F0.imprint","IMPRINT",FACE,{"disambiguationData":[TD([[makeQuery(id+"F0.imprint","IMPRINT",EDGE,{"derivedFrom":sQuery(id+"F0.wireOp",EDGE,"E11.3.30.0")}),-1.0]])]});
            var Q8;
            {var subQ0=sQuery(id+"F0.wireOp",EDGE,"E11.1.31.0");Q8=makeQuery(id+"F0.imprint","IMPRINT",FACE,{"disambiguationData":[TD([[makeQuery(id+"F0.imprint","IMPRINT",EDGE,{"derivedFrom":subQ0}),1.0]])]});}
            var Q9;
            Q9=makeQuery(id+"F0.imprint","IMPRINT",FACE,{"disambiguationData":[TD([[makeQuery(id+"F0.imprint","IMPRINT",EDGE,{"derivedFrom":sQuery(id+"F0.wireOp",EDGE,"E11.3.31.0")}),-1.0]])]});
            var Q10;
            {var subQ0=sQuery(id+"F0.wireOp",EDGE,"E11.1.32.0");Q10=makeQuery(id+"F0.imprint","IMPRINT",FACE,{"disambiguationData":[TD([[makeQuery(id+"F0.imprint","IMPRINT",EDGE,{"derivedFrom":subQ0}),1.0]])]});}
            var Q11;
            Q11=makeQuery(id+"F0.imprint","IMPRINT",FACE,{"disambiguationData":[TD([[makeQuery(id+"F0.imprint","IMPRINT",EDGE,{"derivedFrom":sQuery(id+"F0.wireOp",EDGE,"E11.3.32.0")}),-1.0]])]});
            var Q12;
            {var subQ0=sQuery(id+"F0.wireOp",EDGE,"E11.1.33.0");Q12=makeQuery(id+"F0.imprint","IMPRINT",FACE,{"disambiguationData":[TD([[makeQuery(id+"F0.imprint","IMPRINT",EDGE,{"derivedFrom":subQ0}),1.0]])]});}
            var Q13;
            Q13=makeQuery(id+"F0.imprint","IMPRINT",FACE,{"disambiguationData":[TD([[makeQuery(id+"F0.imprint","IMPRINT",EDGE,{"derivedFrom":sQuery(id+"F0.wireOp",EDGE,"E11.3.33.0")}),-1.0]])]});
            var Q14;
            {var subQ0=sQuery(id+"F0.wireOp",EDGE,"E11.1.34.0");Q14=makeQuery(id+"F0.imprint","IMPRINT",FACE,{"disambiguationData":[TD([[makeQuery(id+"F0.imprint","IMPRINT",EDGE,{"derivedFrom":subQ0}),1.0]])]});}
            var Q15;
            Q15=makeQuery(id+"F0.imprint","IMPRINT",FACE,{"disambiguationData":[TD([[makeQuery(id+"F0.imprint","IMPRINT",EDGE,{"derivedFrom":sQuery(id+"F0.wireOp",EDGE,"E11.3.34.0")}),-1.0]])]});
            var Q16;
            {var subQ0=sQuery(id+"F0.wireOp",EDGE,"E11.1.35.0");Q16=makeQuery(id+"F0.imprint","IMPRINT",FACE,{"disambiguationData":[TD([[makeQuery(id+"F0.imprint","IMPRINT",EDGE,{"derivedFrom":subQ0}),1.0]])]});}
            var Q17;
            Q17=makeQuery(id+"F0.imprint","IMPRINT",FACE,{"disambiguationData":[TD([[makeQuery(id+"F0.imprint","IMPRINT",EDGE,{"derivedFrom":sQuery(id+"F0.wireOp",EDGE,"E11.3.35.0")}),-1.0]])]});
            var Q18;
            {var subQ1=sQuery(id+"F0.wireOp",EDGE,"E3");Q18=makeQuery(id+"F0.imprint","IMPRINT",FACE,{"disambiguationData":[TD([[makeQuery(id+"F0.imprint","IMPRINT",EDGE,{"derivedFrom":subQ1}),1.0]])]});}
            var Q19;
            {var subQ0=sQuery(id+"F0.wireOp",EDGE,"E7.MirrorCS");Q19=makeQuery(id+"F0.imprint","IMPRINT",FACE,{"disambiguationData":[TD([[makeQuery(id+"F0.imprint","IMPRINT",EDGE,{"derivedFrom":subQ0}),1.0]])]});}
            var Q20;
            {var subQ1=sQuery(id+"F0.wireOp",EDGE,"E1");Q20=makeQuery(id+"F0.imprint","IMPRINT",FACE,{"disambiguationData":[TD([[makeQuery(id+"F0.imprint","IMPRINT",EDGE,{"derivedFrom":subQ1}),-1.0]])]});}
            var Q21;
            {var subQ0=sQuery(id+"F0.wireOp",EDGE,"E4");Q21=makeQuery(id+"F0.imprint","IMPRINT",FACE,{"disambiguationData":[TD([[makeQuery(id+"F0.imprint","IMPRINT",EDGE,{"derivedFrom":subQ0}),-1.0]])]});}
            var Q22;
            {var subQ0=sQuery(id+"F0.wireOp",EDGE,"E8.1.0");Q22=makeQuery(id+"F0.imprint","IMPRINT",FACE,{"disambiguationData":[TD([[makeQuery(id+"F0.imprint","IMPRINT",EDGE,{"derivedFrom":subQ0}),1.0]])]});}
            var Q23;
            Q23=makeQuery(id+"F0.imprint","IMPRINT",FACE,{"disambiguationData":[TD([[makeQuery(id+"F0.imprint","IMPRINT",EDGE,{"derivedFrom":sQuery(id+"F0.wireOp",EDGE,"E8.1.1")}),-1.0]])]});
            var Q24;
            {var subQ0=sQuery(id+"F0.wireOp",EDGE,"E8.2.0");Q24=makeQuery(id+"F0.imprint","IMPRINT",FACE,{"disambiguationData":[TD([[makeQuery(id+"F0.imprint","IMPRINT",EDGE,{"derivedFrom":subQ0}),1.0]])]});}
            var Q25;
            Q25=makeQuery(id+"F0.imprint","IMPRINT",FACE,{"disambiguationData":[TD([[makeQuery(id+"F0.imprint","IMPRINT",EDGE,{"derivedFrom":sQuery(id+"F0.wireOp",EDGE,"E8.2.1")}),-1.0]])]});
            var Q26;
            {var subQ0=sQuery(id+"F0.wireOp",EDGE,"E8.3.0");Q26=makeQuery(id+"F0.imprint","IMPRINT",FACE,{"disambiguationData":[TD([[makeQuery(id+"F0.imprint","IMPRINT",EDGE,{"derivedFrom":subQ0}),1.0]])]});}
            var Q27;
            Q27=makeQuery(id+"F0.imprint","IMPRINT",FACE,{"disambiguationData":[TD([[makeQuery(id+"F0.imprint","IMPRINT",EDGE,{"derivedFrom":sQuery(id+"F0.wireOp",EDGE,"E8.3.1")}),-1.0]])]});
            var Q28;
            {var subQ0=sQuery(id+"F0.wireOp",EDGE,"E9.1.4.0");Q28=makeQuery(id+"F0.imprint","IMPRINT",FACE,{"disambiguationData":[TD([[makeQuery(id+"F0.imprint","IMPRINT",EDGE,{"derivedFrom":subQ0}),1.0]])]});}
            var Q29;
            Q29=makeQuery(id+"F0.imprint","IMPRINT",FACE,{"disambiguationData":[TD([[makeQuery(id+"F0.imprint","IMPRINT",EDGE,{"derivedFrom":sQuery(id+"F0.wireOp",EDGE,"E9.3.4.0")}),-1.0]])]});
            var Q30;
            {var subQ0=sQuery(id+"F0.wireOp",EDGE,"E9.1.5.0");Q30=makeQuery(id+"F0.imprint","IMPRINT",FACE,{"disambiguationData":[TD([[makeQuery(id+"F0.imprint","IMPRINT",EDGE,{"derivedFrom":subQ0}),1.0]])]});}
            var Q31;
            Q31=makeQuery(id+"F0.imprint","IMPRINT",FACE,{"disambiguationData":[TD([[makeQuery(id+"F0.imprint","IMPRINT",EDGE,{"derivedFrom":sQuery(id+"F0.wireOp",EDGE,"E9.3.5.0")}),-1.0]])]});
            var Q32;
            {var subQ0=sQuery(id+"F0.wireOp",EDGE,"E9.1.6.0");Q32=makeQuery(id+"F0.imprint","IMPRINT",FACE,{"disambiguationData":[TD([[makeQuery(id+"F0.imprint","IMPRINT",EDGE,{"derivedFrom":subQ0}),1.0]])]});}
            var Q33;
            Q33=makeQuery(id+"F0.imprint","IMPRINT",FACE,{"disambiguationData":[TD([[makeQuery(id+"F0.imprint","IMPRINT",EDGE,{"derivedFrom":sQuery(id+"F0.wireOp",EDGE,"E9.3.6.0")}),-1.0]])]});
            var Q34;
            {var subQ0=sQuery(id+"F0.wireOp",EDGE,"E9.1.7.0");Q34=makeQuery(id+"F0.imprint","IMPRINT",FACE,{"disambiguationData":[TD([[makeQuery(id+"F0.imprint","IMPRINT",EDGE,{"derivedFrom":subQ0}),1.0]])]});}
            var Q35;
            Q35=makeQuery(id+"F0.imprint","IMPRINT",FACE,{"disambiguationData":[TD([[makeQuery(id+"F0.imprint","IMPRINT",EDGE,{"derivedFrom":sQuery(id+"F0.wireOp",EDGE,"E9.3.7.0")}),-1.0]])]});
            var Q36;
            {var subQ0=sQuery(id+"F0.wireOp",EDGE,"E9.1.8.0");Q36=makeQuery(id+"F0.imprint","IMPRINT",FACE,{"disambiguationData":[TD([[makeQuery(id+"F0.imprint","IMPRINT",EDGE,{"derivedFrom":subQ0}),1.0]])]});}
            var Q37;
            Q37=makeQuery(id+"F0.imprint","IMPRINT",FACE,{"disambiguationData":[TD([[makeQuery(id+"F0.imprint","IMPRINT",EDGE,{"derivedFrom":sQuery(id+"F0.wireOp",EDGE,"E9.3.8.0")}),-1.0]])]});
            var Q38;
            {var subQ0=sQuery(id+"F0.wireOp",EDGE,"E9.1.9.0");Q38=makeQuery(id+"F0.imprint","IMPRINT",FACE,{"disambiguationData":[TD([[makeQuery(id+"F0.imprint","IMPRINT",EDGE,{"derivedFrom":subQ0}),1.0]])]});}
            var Q39;
            Q39=makeQuery(id+"F0.imprint","IMPRINT",FACE,{"disambiguationData":[TD([[makeQuery(id+"F0.imprint","IMPRINT",EDGE,{"derivedFrom":sQuery(id+"F0.wireOp",EDGE,"E9.3.9.0")}),-1.0]])]});
            var Q40;
            {var subQ0=sQuery(id+"F0.wireOp",EDGE,"E9.1.10.0");Q40=makeQuery(id+"F0.imprint","IMPRINT",FACE,{"disambiguationData":[TD([[makeQuery(id+"F0.imprint","IMPRINT",EDGE,{"derivedFrom":subQ0}),1.0]])]});}
            var Q41;
            Q41=makeQuery(id+"F0.imprint","IMPRINT",FACE,{"disambiguationData":[TD([[makeQuery(id+"F0.imprint","IMPRINT",EDGE,{"derivedFrom":sQuery(id+"F0.wireOp",EDGE,"E9.3.10.0")}),-1.0]])]});
            var Q42;
            {var subQ0=sQuery(id+"F0.wireOp",EDGE,"E9.1.11.0");Q42=makeQuery(id+"F0.imprint","IMPRINT",FACE,{"disambiguationData":[TD([[makeQuery(id+"F0.imprint","IMPRINT",EDGE,{"derivedFrom":subQ0}),1.0]])]});}
            var Q43;
            Q43=makeQuery(id+"F0.imprint","IMPRINT",FACE,{"disambiguationData":[TD([[makeQuery(id+"F0.imprint","IMPRINT",EDGE,{"derivedFrom":sQuery(id+"F0.wireOp",EDGE,"E9.3.11.0")}),-1.0]])]});
            var Q44;
            {var subQ0=sQuery(id+"F0.wireOp",EDGE,"E10.1.12.0");Q44=makeQuery(id+"F0.imprint","IMPRINT",FACE,{"disambiguationData":[TD([[makeQuery(id+"F0.imprint","IMPRINT",EDGE,{"derivedFrom":subQ0}),1.0]])]});}
            var Q45;
            Q45=makeQuery(id+"F0.imprint","IMPRINT",FACE,{"disambiguationData":[TD([[makeQuery(id+"F0.imprint","IMPRINT",EDGE,{"derivedFrom":sQuery(id+"F0.wireOp",EDGE,"E10.3.12.0")}),-1.0]])]});
            var Q46;
            {var subQ0=sQuery(id+"F0.wireOp",EDGE,"E10.1.13.0");Q46=makeQuery(id+"F0.imprint","IMPRINT",FACE,{"disambiguationData":[TD([[makeQuery(id+"F0.imprint","IMPRINT",EDGE,{"derivedFrom":subQ0}),1.0]])]});}
            var Q47;
            Q47=makeQuery(id+"F0.imprint","IMPRINT",FACE,{"disambiguationData":[TD([[makeQuery(id+"F0.imprint","IMPRINT",EDGE,{"derivedFrom":sQuery(id+"F0.wireOp",EDGE,"E10.3.13.0")}),-1.0]])]});
            var Q48;
            {var subQ0=sQuery(id+"F0.wireOp",EDGE,"E10.1.14.0");Q48=makeQuery(id+"F0.imprint","IMPRINT",FACE,{"disambiguationData":[TD([[makeQuery(id+"F0.imprint","IMPRINT",EDGE,{"derivedFrom":subQ0}),1.0]])]});}
            var Q49;
            Q49=makeQuery(id+"F0.imprint","IMPRINT",FACE,{"disambiguationData":[TD([[makeQuery(id+"F0.imprint","IMPRINT",EDGE,{"derivedFrom":sQuery(id+"F0.wireOp",EDGE,"E10.3.14.0")}),-1.0]])]});
            var Q50;
            {var subQ0=sQuery(id+"F0.wireOp",EDGE,"E10.1.15.0");Q50=makeQuery(id+"F0.imprint","IMPRINT",FACE,{"disambiguationData":[TD([[makeQuery(id+"F0.imprint","IMPRINT",EDGE,{"derivedFrom":subQ0}),1.0]])]});}
            var Q51;
            Q51=makeQuery(id+"F0.imprint","IMPRINT",FACE,{"disambiguationData":[TD([[makeQuery(id+"F0.imprint","IMPRINT",EDGE,{"derivedFrom":sQuery(id+"F0.wireOp",EDGE,"E10.3.15.0")}),-1.0]])]});
            var Q52;
            {var subQ0=sQuery(id+"F0.wireOp",EDGE,"E10.1.16.0");Q52=makeQuery(id+"F0.imprint","IMPRINT",FACE,{"disambiguationData":[TD([[makeQuery(id+"F0.imprint","IMPRINT",EDGE,{"derivedFrom":subQ0}),1.0]])]});}
            var Q53;
            Q53=makeQuery(id+"F0.imprint","IMPRINT",FACE,{"disambiguationData":[TD([[makeQuery(id+"F0.imprint","IMPRINT",EDGE,{"derivedFrom":sQuery(id+"F0.wireOp",EDGE,"E10.3.16.0")}),-1.0]])]});
            var Q54;
            {var subQ0=sQuery(id+"F0.wireOp",EDGE,"E10.1.17.0");Q54=makeQuery(id+"F0.imprint","IMPRINT",FACE,{"disambiguationData":[TD([[makeQuery(id+"F0.imprint","IMPRINT",EDGE,{"derivedFrom":subQ0}),1.0]])]});}
            var Q55;
            Q55=makeQuery(id+"F0.imprint","IMPRINT",FACE,{"disambiguationData":[TD([[makeQuery(id+"F0.imprint","IMPRINT",EDGE,{"derivedFrom":sQuery(id+"F0.wireOp",EDGE,"E10.3.17.0")}),-1.0]])]});
            var Q56;
            {var subQ0=sQuery(id+"F0.wireOp",EDGE,"E10.1.18.0");Q56=makeQuery(id+"F0.imprint","IMPRINT",FACE,{"disambiguationData":[TD([[makeQuery(id+"F0.imprint","IMPRINT",EDGE,{"derivedFrom":subQ0}),1.0]])]});}
            var Q57;
            Q57=makeQuery(id+"F0.imprint","IMPRINT",FACE,{"disambiguationData":[TD([[makeQuery(id+"F0.imprint","IMPRINT",EDGE,{"derivedFrom":sQuery(id+"F0.wireOp",EDGE,"E10.3.18.0")}),-1.0]])]});
            var Q58;
            {var subQ0=sQuery(id+"F0.wireOp",EDGE,"E10.1.19.0");Q58=makeQuery(id+"F0.imprint","IMPRINT",FACE,{"disambiguationData":[TD([[makeQuery(id+"F0.imprint","IMPRINT",EDGE,{"derivedFrom":subQ0}),1.0]])]});}
            var Q59;
            Q59=makeQuery(id+"F0.imprint","IMPRINT",FACE,{"disambiguationData":[TD([[makeQuery(id+"F0.imprint","IMPRINT",EDGE,{"derivedFrom":sQuery(id+"F0.wireOp",EDGE,"E10.3.19.0")}),-1.0]])]});
            var Q60;
            {var subQ0=sQuery(id+"F0.wireOp",EDGE,"E10.1.20.0");Q60=makeQuery(id+"F0.imprint","IMPRINT",FACE,{"disambiguationData":[TD([[makeQuery(id+"F0.imprint","IMPRINT",EDGE,{"derivedFrom":subQ0}),1.0]])]});}
            var Q61;
            Q61=makeQuery(id+"F0.imprint","IMPRINT",FACE,{"disambiguationData":[TD([[makeQuery(id+"F0.imprint","IMPRINT",EDGE,{"derivedFrom":sQuery(id+"F0.wireOp",EDGE,"E10.3.20.0")}),-1.0]])]});
            var Q62;
            {var subQ0=sQuery(id+"F0.wireOp",EDGE,"E10.1.21.0");Q62=makeQuery(id+"F0.imprint","IMPRINT",FACE,{"disambiguationData":[TD([[makeQuery(id+"F0.imprint","IMPRINT",EDGE,{"derivedFrom":subQ0}),1.0]])]});}
            var Q63;
            Q63=makeQuery(id+"F0.imprint","IMPRINT",FACE,{"disambiguationData":[TD([[makeQuery(id+"F0.imprint","IMPRINT",EDGE,{"derivedFrom":sQuery(id+"F0.wireOp",EDGE,"E10.3.21.0")}),-1.0]])]});
            var Q64;
            {var subQ0=sQuery(id+"F0.wireOp",EDGE,"E10.1.22.0");Q64=makeQuery(id+"F0.imprint","IMPRINT",FACE,{"disambiguationData":[TD([[makeQuery(id+"F0.imprint","IMPRINT",EDGE,{"derivedFrom":subQ0}),1.0]])]});}
            var Q65;
            Q65=makeQuery(id+"F0.imprint","IMPRINT",FACE,{"disambiguationData":[TD([[makeQuery(id+"F0.imprint","IMPRINT",EDGE,{"derivedFrom":sQuery(id+"F0.wireOp",EDGE,"E10.3.22.0")}),-1.0]])]});
            var Q66;
            {var subQ0=sQuery(id+"F0.wireOp",EDGE,"E10.1.23.0");Q66=makeQuery(id+"F0.imprint","IMPRINT",FACE,{"disambiguationData":[TD([[makeQuery(id+"F0.imprint","IMPRINT",EDGE,{"derivedFrom":subQ0}),1.0]])]});}
            var Q67;
            Q67=makeQuery(id+"F0.imprint","IMPRINT",FACE,{"disambiguationData":[TD([[makeQuery(id+"F0.imprint","IMPRINT",EDGE,{"derivedFrom":sQuery(id+"F0.wireOp",EDGE,"E10.3.23.0")}),-1.0]])]});
            var Q68;
            {var subQ0=sQuery(id+"F0.wireOp",EDGE,"E11.1.24.0");Q68=makeQuery(id+"F0.imprint","IMPRINT",FACE,{"disambiguationData":[TD([[makeQuery(id+"F0.imprint","IMPRINT",EDGE,{"derivedFrom":subQ0}),1.0]])]});}
            var Q69;
            Q69=makeQuery(id+"F0.imprint","IMPRINT",FACE,{"disambiguationData":[TD([[makeQuery(id+"F0.imprint","IMPRINT",EDGE,{"derivedFrom":sQuery(id+"F0.wireOp",EDGE,"E11.3.24.0")}),-1.0]])]});
            var Q70;
            {var subQ0=sQuery(id+"F0.wireOp",EDGE,"E11.1.25.0");Q70=makeQuery(id+"F0.imprint","IMPRINT",FACE,{"disambiguationData":[TD([[makeQuery(id+"F0.imprint","IMPRINT",EDGE,{"derivedFrom":subQ0}),1.0]])]});}
            var Q71;
            Q71=makeQuery(id+"F0.imprint","IMPRINT",FACE,{"disambiguationData":[TD([[makeQuery(id+"F0.imprint","IMPRINT",EDGE,{"derivedFrom":sQuery(id+"F0.wireOp",EDGE,"E11.3.25.0")}),-1.0]])]});
            var Q72;
            {var subQ0=sQuery(id+"F0.wireOp",EDGE,"E11.1.26.0");Q72=makeQuery(id+"F0.imprint","IMPRINT",FACE,{"disambiguationData":[TD([[makeQuery(id+"F0.imprint","IMPRINT",EDGE,{"derivedFrom":subQ0}),1.0]])]});}
            var Q73;
            Q73=makeQuery(id+"F0.imprint","IMPRINT",FACE,{"disambiguationData":[TD([[makeQuery(id+"F0.imprint","IMPRINT",EDGE,{"derivedFrom":sQuery(id+"F0.wireOp",EDGE,"E11.3.26.0")}),-1.0]])]});
            var Q74;
            {var subQ0=sQuery(id+"F0.wireOp",EDGE,"E11.1.27.0");Q74=makeQuery(id+"F0.imprint","IMPRINT",FACE,{"disambiguationData":[TD([[makeQuery(id+"F0.imprint","IMPRINT",EDGE,{"derivedFrom":subQ0}),1.0]])]});}
            extrude(context, id + "F1", {"entities" : qUnion([Q0, Q1, Q2, Q3, Q4, Q5, Q6, Q7, Q8, Q9, Q10, Q11, Q12, Q13, Q14, Q15, Q16, Q17, Q18, Q19, Q20, Q21, Q22, Q23, Q24, Q25, Q26, Q27, Q28, Q29, Q30, Q31, Q32, Q33, Q34, Q35, Q36, Q37, Q38, Q39, Q40, Q41, Q42, Q43, Q44, Q45, Q46, Q47, Q48, Q49, Q50, Q51, Q52, Q53, Q54, Q55, Q56, Q57, Q58, Q59, Q60, Q61, Q62, Q63, Q64, Q65, Q66, Q67, Q68, Q69, Q70, Q71, Q72, Q73, Q74]), "depth" : 23.63 * mm});
        }
        {
            var Q0;
            Q0=makeQuery(id+"F1.opExtrude","CAP_FACE",FACE,{"disambiguationData":[OSD([sQuery(id+"F0.wireOp",EDGE,"E0"),sQuery(id+"F0.wireOp",EDGE,"E1"),sQuery(id+"F0.wireOp",EDGE,"E2"),sQuery(id+"F0.wireOp",EDGE,"E5.MirrorCS"),sQuery(id+"F0.wireOp",EDGE,"E6.MirrorCS"),sQuery(id+"F0.wireOp",EDGE,"E8.1.0"),sQuery(id+"F0.wireOp",EDGE,"E8.1.1"),sQuery(id+"F0.wireOp",EDGE,"E8.1.3"),sQuery(id+"F0.wireOp",EDGE,"E8.1.4"),sQuery(id+"F0.wireOp",EDGE,"E8.2.0"),sQuery(id+"F0.wireOp",EDGE,"E8.2.1"),sQuery(id+"F0.wireOp",EDGE,"E8.2.3"),sQuery(id+"F0.wireOp",EDGE,"E8.2.4"),sQuery(id+"F0.wireOp",EDGE,"E8.3.0"),sQuery(id+"F0.wireOp",EDGE,"E8.3.1"),sQuery(id+"F0.wireOp",EDGE,"E8.3.3"),sQuery(id+"F0.wireOp",EDGE,"E8.3.4"),sQuery(id+"F0.wireOp",EDGE,"E9.1.4.0"),sQuery(id+"F0.wireOp",EDGE,"E9.3.4.0"),sQuery(id+"F0.wireOp",EDGE,"E9.9.4.0"),sQuery(id+"F0.wireOp",EDGE,"E9.12.4.0"),sQuery(id+"F0.wireOp",EDGE,"E9.1.5.0"),sQuery(id+"F0.wireOp",EDGE,"E9.3.5.0"),sQuery(id+"F0.wireOp",EDGE,"E9.9.5.0"),sQuery(id+"F0.wireOp",EDGE,"E9.12.5.0"),sQuery(id+"F0.wireOp",EDGE,"E9.1.6.0"),sQuery(id+"F0.wireOp",EDGE,"E9.3.6.0"),sQuery(id+"F0.wireOp",EDGE,"E9.9.6.0"),sQuery(id+"F0.wireOp",EDGE,"E9.12.6.0"),sQuery(id+"F0.wireOp",EDGE,"E9.1.7.0"),sQuery(id+"F0.wireOp",EDGE,"E9.3.7.0"),sQuery(id+"F0.wireOp",EDGE,"E9.9.7.0"),sQuery(id+"F0.wireOp",EDGE,"E9.12.7.0"),sQuery(id+"F0.wireOp",EDGE,"E9.1.8.0"),sQuery(id+"F0.wireOp",EDGE,"E9.3.8.0"),sQuery(id+"F0.wireOp",EDGE,"E9.9.8.0"),sQuery(id+"F0.wireOp",EDGE,"E9.12.8.0"),sQuery(id+"F0.wireOp",EDGE,"E9.1.9.0"),sQuery(id+"F0.wireOp",EDGE,"E9.3.9.0"),sQuery(id+"F0.wireOp",EDGE,"E9.9.9.0"),sQuery(id+"F0.wireOp",EDGE,"E9.12.9.0"),sQuery(id+"F0.wireOp",EDGE,"E9.1.10.0"),sQuery(id+"F0.wireOp",EDGE,"E9.3.10.0"),sQuery(id+"F0.wireOp",EDGE,"E9.9.10.0"),sQuery(id+"F0.wireOp",EDGE,"E9.12.10.0"),sQuery(id+"F0.wireOp",EDGE,"E9.1.11.0"),sQuery(id+"F0.wireOp",EDGE,"E9.3.11.0"),sQuery(id+"F0.wireOp",EDGE,"E9.9.11.0"),sQuery(id+"F0.wireOp",EDGE,"E9.12.11.0"),sQuery(id+"F0.wireOp",EDGE,"E10.1.12.0"),sQuery(id+"F0.wireOp",EDGE,"E10.3.12.0"),sQuery(id+"F0.wireOp",EDGE,"E10.9.12.0"),sQuery(id+"F0.wireOp",EDGE,"E10.12.12.0"),sQuery(id+"F0.wireOp",EDGE,"E10.1.13.0"),sQuery(id+"F0.wireOp",EDGE,"E10.3.13.0"),sQuery(id+"F0.wireOp",EDGE,"E10.9.13.0"),sQuery(id+"F0.wireOp",EDGE,"E10.12.13.0"),sQuery(id+"F0.wireOp",EDGE,"E10.1.14.0"),sQuery(id+"F0.wireOp",EDGE,"E10.3.14.0"),sQuery(id+"F0.wireOp",EDGE,"E10.9.14.0"),sQuery(id+"F0.wireOp",EDGE,"E10.12.14.0"),sQuery(id+"F0.wireOp",EDGE,"E10.1.15.0"),sQuery(id+"F0.wireOp",EDGE,"E10.3.15.0"),sQuery(id+"F0.wireOp",EDGE,"E10.9.15.0"),sQuery(id+"F0.wireOp",EDGE,"E10.12.15.0"),sQuery(id+"F0.wireOp",EDGE,"E10.1.16.0"),sQuery(id+"F0.wireOp",EDGE,"E10.3.16.0"),sQuery(id+"F0.wireOp",EDGE,"E10.9.16.0"),sQuery(id+"F0.wireOp",EDGE,"E10.12.16.0"),sQuery(id+"F0.wireOp",EDGE,"E10.1.17.0"),sQuery(id+"F0.wireOp",EDGE,"E10.3.17.0"),sQuery(id+"F0.wireOp",EDGE,"E10.9.17.0"),sQuery(id+"F0.wireOp",EDGE,"E10.12.17.0"),sQuery(id+"F0.wireOp",EDGE,"E10.1.18.0"),sQuery(id+"F0.wireOp",EDGE,"E10.3.18.0"),sQuery(id+"F0.wireOp",EDGE,"E10.9.18.0"),sQuery(id+"F0.wireOp",EDGE,"E10.12.18.0"),sQuery(id+"F0.wireOp",EDGE,"E10.1.19.0"),sQuery(id+"F0.wireOp",EDGE,"E10.3.19.0"),sQuery(id+"F0.wireOp",EDGE,"E10.9.19.0"),sQuery(id+"F0.wireOp",EDGE,"E10.12.19.0"),sQuery(id+"F0.wireOp",EDGE,"E10.1.20.0"),sQuery(id+"F0.wireOp",EDGE,"E10.3.20.0"),sQuery(id+"F0.wireOp",EDGE,"E10.9.20.0"),sQuery(id+"F0.wireOp",EDGE,"E10.12.20.0"),sQuery(id+"F0.wireOp",EDGE,"E10.1.21.0"),sQuery(id+"F0.wireOp",EDGE,"E10.3.21.0"),sQuery(id+"F0.wireOp",EDGE,"E10.9.21.0"),sQuery(id+"F0.wireOp",EDGE,"E10.12.21.0"),sQuery(id+"F0.wireOp",EDGE,"E10.1.22.0"),sQuery(id+"F0.wireOp",EDGE,"E10.3.22.0"),sQuery(id+"F0.wireOp",EDGE,"E10.9.22.0"),sQuery(id+"F0.wireOp",EDGE,"E10.12.22.0"),sQuery(id+"F0.wireOp",EDGE,"E10.1.23.0"),sQuery(id+"F0.wireOp",EDGE,"E10.3.23.0"),sQuery(id+"F0.wireOp",EDGE,"E10.9.23.0"),sQuery(id+"F0.wireOp",EDGE,"E10.12.23.0"),sQuery(id+"F0.wireOp",EDGE,"E11.1.24.0"),sQuery(id+"F0.wireOp",EDGE,"E11.3.24.0"),sQuery(id+"F0.wireOp",EDGE,"E11.9.24.0"),sQuery(id+"F0.wireOp",EDGE,"E11.12.24.0"),sQuery(id+"F0.wireOp",EDGE,"E11.1.25.0"),sQuery(id+"F0.wireOp",EDGE,"E11.3.25.0"),sQuery(id+"F0.wireOp",EDGE,"E11.9.25.0"),sQuery(id+"F0.wireOp",EDGE,"E11.12.25.0"),sQuery(id+"F0.wireOp",EDGE,"E11.1.26.0"),sQuery(id+"F0.wireOp",EDGE,"E11.3.26.0"),sQuery(id+"F0.wireOp",EDGE,"E11.9.26.0"),sQuery(id+"F0.wireOp",EDGE,"E11.12.26.0"),sQuery(id+"F0.wireOp",EDGE,"E11.1.27.0"),sQuery(id+"F0.wireOp",EDGE,"E11.3.27.0"),sQuery(id+"F0.wireOp",EDGE,"E11.9.27.0"),sQuery(id+"F0.wireOp",EDGE,"E11.12.27.0"),sQuery(id+"F0.wireOp",EDGE,"E11.1.28.0"),sQuery(id+"F0.wireOp",EDGE,"E11.3.28.0"),sQuery(id+"F0.wireOp",EDGE,"E11.9.28.0"),sQuery(id+"F0.wireOp",EDGE,"E11.12.28.0"),sQuery(id+"F0.wireOp",EDGE,"E11.1.29.0"),sQuery(id+"F0.wireOp",EDGE,"E11.3.29.0"),sQuery(id+"F0.wireOp",EDGE,"E11.9.29.0"),sQuery(id+"F0.wireOp",EDGE,"E11.12.29.0"),sQuery(id+"F0.wireOp",EDGE,"E11.1.30.0"),sQuery(id+"F0.wireOp",EDGE,"E11.3.30.0"),sQuery(id+"F0.wireOp",EDGE,"E11.9.30.0"),sQuery(id+"F0.wireOp",EDGE,"E11.12.30.0"),sQuery(id+"F0.wireOp",EDGE,"E11.1.31.0"),sQuery(id+"F0.wireOp",EDGE,"E11.3.31.0"),sQuery(id+"F0.wireOp",EDGE,"E11.9.31.0"),sQuery(id+"F0.wireOp",EDGE,"E11.12.31.0"),sQuery(id+"F0.wireOp",EDGE,"E11.1.32.0"),sQuery(id+"F0.wireOp",EDGE,"E11.3.32.0"),sQuery(id+"F0.wireOp",EDGE,"E11.9.32.0"),sQuery(id+"F0.wireOp",EDGE,"E11.12.32.0"),sQuery(id+"F0.wireOp",EDGE,"E11.1.33.0"),sQuery(id+"F0.wireOp",EDGE,"E11.3.33.0"),sQuery(id+"F0.wireOp",EDGE,"E11.9.33.0"),sQuery(id+"F0.wireOp",EDGE,"E11.12.33.0"),sQuery(id+"F0.wireOp",EDGE,"E11.1.34.0"),sQuery(id+"F0.wireOp",EDGE,"E11.3.34.0"),sQuery(id+"F0.wireOp",EDGE,"E11.9.34.0"),sQuery(id+"F0.wireOp",EDGE,"E11.12.34.0"),sQuery(id+"F0.wireOp",EDGE,"E11.1.35.0"),sQuery(id+"F0.wireOp",EDGE,"E11.3.35.0"),sQuery(id+"F0.wireOp",EDGE,"E11.9.35.0"),sQuery(id+"F0.wireOp",EDGE,"E11.12.35.0"),sQuery(id+"F0.wireOp",EDGE,"E12"),sQuery(id+"F0.wireOp",EDGE,"E13.rect.bottom"),sQuery(id+"F0.wireOp",EDGE,"E13.rect.top"),sQuery(id+"F0.wireOp",EDGE,"E13.rect.left"),sQuery(id+"F0.wireOp",EDGE,"E13.rect.right"),sQuery(id+"F0.wireOp",EDGE,"E14.rect.bottom"),sQuery(id+"F0.wireOp",EDGE,"E14.rect.top"),sQuery(id+"F0.wireOp",EDGE,"E14.rect.right"),sQuery(id+"F0.wireOp",EDGE,"E15.trimOffspring"),sQuery(id+"F0.wireOp",EDGE,"E16.trimOffspring"),sQuery(id+"F0.wireOp",EDGE,"E17.trimOffspring"),sQuery(id+"F0.wireOp",EDGE,"E18.trimOffspring"),sQuery(id+"F0.wireOp",EDGE,"E19.trimOffspring"),sQuery(id+"F0.wireOp",EDGE,"E20.trimOffspring"),sQuery(id+"F0.wireOp",EDGE,"E21.trimOffspring"),sQuery(id+"F0.wireOp",EDGE,"E22"),sQuery(id+"F0.wireOp",EDGE,"E23.1.0"),sQuery(id+"F0.wireOp",EDGE,"E23.1.1"),sQuery(id+"F0.wireOp",EDGE,"E23.1.2"),sQuery(id+"F0.wireOp",EDGE,"E23.1.3"),sQuery(id+"F0.wireOp",EDGE,"E23.1.4"),sQuery(id+"F0.wireOp",EDGE,"E23.1.5"),sQuery(id+"F0.wireOp",EDGE,"E23.1.7"),sQuery(id+"F0.wireOp",EDGE,"E23.1.8"),sQuery(id+"F0.wireOp",EDGE,"E23.1.10"),sQuery(id+"F0.wireOp",EDGE,"E23.1.11"),sQuery(id+"F0.wireOp",EDGE,"E23.1.12"),sQuery(id+"F0.wireOp",EDGE,"E23.1.13"),sQuery(id+"F0.wireOp",EDGE,"E23.1.14"),sQuery(id+"F0.wireOp",EDGE,"E23.1.15"),sQuery(id+"F0.wireOp",EDGE,"E23.1.16"),sQuery(id+"F0.wireOp",EDGE,"E23.1.17"),sQuery(id+"F0.wireOp",EDGE,"E23.2.0"),sQuery(id+"F0.wireOp",EDGE,"E23.2.1"),sQuery(id+"F0.wireOp",EDGE,"E23.2.2"),sQuery(id+"F0.wireOp",EDGE,"E23.2.3"),sQuery(id+"F0.wireOp",EDGE,"E23.2.4"),sQuery(id+"F0.wireOp",EDGE,"E23.2.5"),sQuery(id+"F0.wireOp",EDGE,"E23.2.7"),sQuery(id+"F0.wireOp",EDGE,"E23.2.8"),sQuery(id+"F0.wireOp",EDGE,"E23.2.10"),sQuery(id+"F0.wireOp",EDGE,"E23.2.11"),sQuery(id+"F0.wireOp",EDGE,"E23.2.12"),sQuery(id+"F0.wireOp",EDGE,"E23.2.13"),sQuery(id+"F0.wireOp",EDGE,"E23.2.14"),sQuery(id+"F0.wireOp",EDGE,"E23.2.15"),sQuery(id+"F0.wireOp",EDGE,"E23.2.16"),sQuery(id+"F0.wireOp",EDGE,"E23.2.17"),sQuery(id+"F0.wireOp",EDGE,"E23.3.0"),sQuery(id+"F0.wireOp",EDGE,"E23.3.1"),sQuery(id+"F0.wireOp",EDGE,"E23.3.2"),sQuery(id+"F0.wireOp",EDGE,"E23.3.3"),sQuery(id+"F0.wireOp",EDGE,"E23.3.4"),sQuery(id+"F0.wireOp",EDGE,"E23.3.5"),sQuery(id+"F0.wireOp",EDGE,"E23.3.7"),sQuery(id+"F0.wireOp",EDGE,"E23.3.8"),sQuery(id+"F0.wireOp",EDGE,"E23.3.10"),sQuery(id+"F0.wireOp",EDGE,"E23.3.11"),sQuery(id+"F0.wireOp",EDGE,"E23.3.12"),sQuery(id+"F0.wireOp",EDGE,"E23.3.13"),sQuery(id+"F0.wireOp",EDGE,"E23.3.14"),sQuery(id+"F0.wireOp",EDGE,"E23.3.15"),sQuery(id+"F0.wireOp",EDGE,"E23.3.16"),sQuery(id+"F0.wireOp",EDGE,"E23.3.17"),sQuery(id+"F0.wireOp",EDGE,"E23.4.0"),sQuery(id+"F0.wireOp",EDGE,"E23.4.1"),sQuery(id+"F0.wireOp",EDGE,"E23.4.2"),sQuery(id+"F0.wireOp",EDGE,"E23.4.3"),sQuery(id+"F0.wireOp",EDGE,"E23.4.4"),sQuery(id+"F0.wireOp",EDGE,"E23.4.5"),sQuery(id+"F0.wireOp",EDGE,"E23.4.7"),sQuery(id+"F0.wireOp",EDGE,"E23.4.8"),sQuery(id+"F0.wireOp",EDGE,"E23.4.10"),sQuery(id+"F0.wireOp",EDGE,"E23.4.11"),sQuery(id+"F0.wireOp",EDGE,"E23.4.12"),sQuery(id+"F0.wireOp",EDGE,"E23.4.13"),sQuery(id+"F0.wireOp",EDGE,"E23.4.14"),sQuery(id+"F0.wireOp",EDGE,"E23.4.15"),sQuery(id+"F0.wireOp",EDGE,"E23.4.16"),sQuery(id+"F0.wireOp",EDGE,"E23.4.17"),sQuery(id+"F0.wireOp",EDGE,"E23.5.0"),sQuery(id+"F0.wireOp",EDGE,"E23.5.1"),sQuery(id+"F0.wireOp",EDGE,"E23.5.2"),sQuery(id+"F0.wireOp",EDGE,"E23.5.3"),sQuery(id+"F0.wireOp",EDGE,"E23.5.4"),sQuery(id+"F0.wireOp",EDGE,"E23.5.5"),sQuery(id+"F0.wireOp",EDGE,"E23.5.7"),sQuery(id+"F0.wireOp",EDGE,"E23.5.8"),sQuery(id+"F0.wireOp",EDGE,"E23.5.10"),sQuery(id+"F0.wireOp",EDGE,"E23.5.11"),sQuery(id+"F0.wireOp",EDGE,"E23.5.12"),sQuery(id+"F0.wireOp",EDGE,"E23.5.13"),sQuery(id+"F0.wireOp",EDGE,"E23.5.14"),sQuery(id+"F0.wireOp",EDGE,"E23.5.15"),sQuery(id+"F0.wireOp",EDGE,"E23.5.16"),sQuery(id+"F0.wireOp",EDGE,"E23.5.17")])],"isStart":false});
            var sketch = newSketch(context, id + "F2", { "sketchPlane" : qUnion([Q0])});
            skCircle(sketch, "E24", {"center": v(0, 0) * mm, "radius": 39.15 * mm});
            skSolve(sketch);
        }
        {
            var Q0;
            Q0 = qSketchRegion(id + "F2", true);
            extrude(context, id + "F3", {"entities" : qUnion([Q0]), "operationType" : NewBodyOperationType.REMOVE, "oppositeDirection" : true, "depth" : 10.63 * mm});
        }
        {
            var Q0;
            Q0=makeQuery(id+"F3.boolean.opBoolean","COPY",FACE,{"derivedFrom":makeQuery(id+"F3.opExtrude","CAP_FACE",FACE,{"disambiguationData":[OSD([sQuery(id+"F2.wireOp",EDGE,"E24")])],"isStart":false})});
            var sketch = newSketch(context, id + "F4", { "sketchPlane" : qUnion([Q0])});
            skCircle(sketch, "E25", {"center": v(0, 0) * mm, "radius": 17.52 * mm});
            skCircle(sketch, "E26.0", {"center": v(0, 0) * mm, "radius": 11.63 * mm});
            skSolve(sketch);
        }
        {
            var Q0;
            Q0=makeQuery(id+"F4.imprint","IMPRINT",FACE,{"disambiguationData":[TD([[makeQuery(id+"F4.imprint","IMPRINT",EDGE,{"derivedFrom":sQuery(id+"F4.wireOp",EDGE,"E25")}),1.0]])]});
            extrude(context, id + "F5", {"entities" : qUnion([Q0]), "operationType" : NewBodyOperationType.ADD, "depth" : 6.8 * mm});
        }
        {
            var Q0;
            Q0=makeQuery(id+"F5.boolean.opBoolean","SPLIT",FACE,{"disambiguationData":[TD([makeQuery(id+"F5.opExtrude","SWEPT_FACE",FACE,{"disambiguationData":[OSD([sQuery(id+"F4.wireOp",EDGE,"E26.0")])]})])],"derivedFrom":makeQuery(id+"F3.boolean.opBoolean","COPY",FACE,{"derivedFrom":makeQuery(id+"F3.opExtrude","CAP_FACE",FACE,{"disambiguationData":[OSD([sQuery(id+"F2.wireOp",EDGE,"E24")])],"isStart":false})})});
            var sketch = newSketch(context, id + "F6", { "sketchPlane" : qUnion([Q0])});
            skCircle(sketch, "E27.cCircle", {"center": v(0, 0) * mm, "radius": 9.5 * mm, "construction": true});
            skLineSegment(sketch, "E27.0", {"start": v(0, -9.5) * mm, "end": v(-8.22, -4.75) * mm});
            skLineSegment(sketch, "E27.1", {"start": v(-8.22, -4.75) * mm, "end": v(-8.22, 4.75) * mm});
            skLineSegment(sketch, "E27.2", {"start": v(-8.22, 4.75) * mm, "end": v(0, 9.5) * mm});
            skLineSegment(sketch, "E27.3", {"start": v(0, 9.5) * mm, "end": v(8.22, 4.75) * mm});
            skLineSegment(sketch, "E27.4", {"start": v(8.22, 4.75) * mm, "end": v(8.22, -4.75) * mm});
            skLineSegment(sketch, "E27.5", {"start": v(8.22, -4.75) * mm, "end": v(0, -9.5) * mm});
            skSolve(sketch);
        }
        {
            var Q0;
            Q0=makeQuery(id+"F6.imprint","IMPRINT",FACE,{"disambiguationData":[TD([[makeQuery(id+"F6.imprint","IMPRINT",EDGE,{"derivedFrom":sQuery(id+"F6.wireOp",EDGE,"E27.0")}),-1.0]])]});
            extrude(context, id + "F7", {"entities" : qUnion([Q0]), "operationType" : NewBodyOperationType.REMOVE, "oppositeDirection" : true, "depth" : 25.4 * mm});
        }
    });
